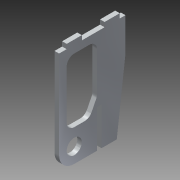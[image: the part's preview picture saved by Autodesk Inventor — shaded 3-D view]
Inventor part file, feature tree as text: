
AUTODESK INVENTOR PART (.ipt)
format: ipt  version: 2015 (Build 190159000, 159)  size: 150,016 bytes
history: native  units: mm
features: extrude x1, sketch x1
ambient origin geometry x8: Origin, YZ Plane, XZ Plane, XY Plane, X Axis, Y Axis, Z Axis, Center Point
bodies: Body1 (feature_tree)
feature tree (2):
  extrude  "Extrusion2"  Depth=10.0mm
  sketch  "Sketch1"  dims[d5=50.0mm d6=66.5mm d7=10.0mm d10=5.0mm d12=10.0mm d17=10.0mm d18=3.0mm d20=10.0mm d21=3.0mm d22=5.0mm d23=15.0mm d24=3.0mm d25=3.0mm d42=3.0mm d46=3.75mm d47=22.0mm d49=2.0mm d54=10.0mm d55=15.0mm d57=68.0mm d58=15.75mm d59=25.0mm d61=5.0mm d65=5.0mm d66=10.0mm d67=5.0mm d68=5.0mm d69=3.0mm d70=0.0mm]
